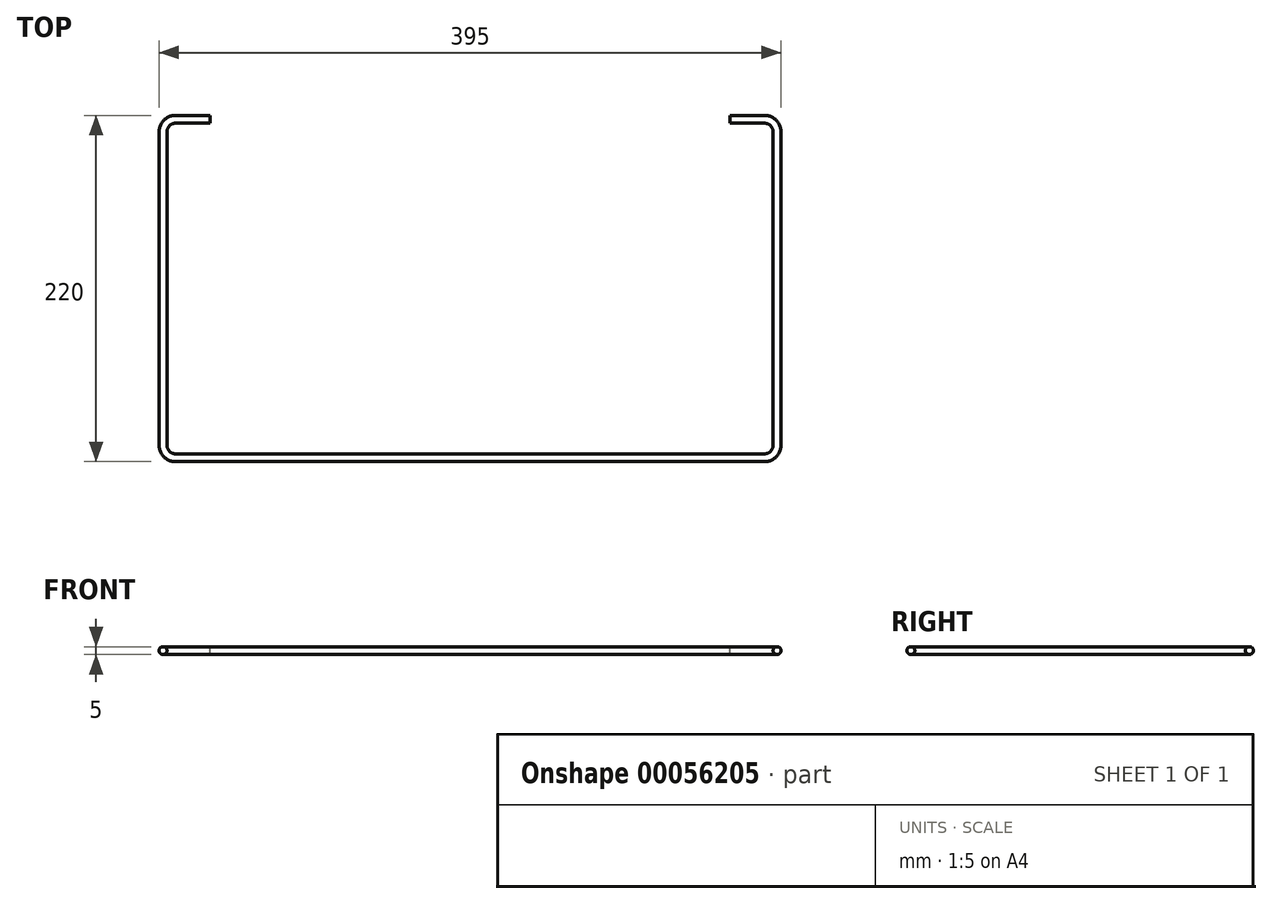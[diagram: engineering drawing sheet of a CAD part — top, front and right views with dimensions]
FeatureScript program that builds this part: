
annotation { "Feature Type Name" : "Feature", "Feature Type Description" : "" }
export const myFeature = defineFeature(function(context is Context, id is Id, definition is map)
    precondition{}
    {
        {
            var Q0;
            Q0=qCreatedBy(makeId("Top.planeOp"),FACE);
            var sketch = newSketch(context, id + "F0", { "sketchPlane" : qUnion([Q0])});
            skLineSegment(sketch, "E0.top", {"start": v(-22, -215) * mm, "end": v(352, -215) * mm});
            skLineSegment(sketch, "E0.left", {"start": v(-30, -8) * mm, "end": v(-30, -207) * mm});
            skLineSegment(sketch, "E0.right", {"start": v(360, -8) * mm, "end": v(360, -207) * mm});
            skPoint(sketch, "E1.visualSharp", {"position": v(-30, -215) * mm});
            skArc(sketch, "E1.filletArc", {"start": v(-30, -207) * mm, "mid": v(-27.66, -212.66) * mm, "end": v(-22, -215) * mm});
            skPoint(sketch, "E2.visualSharp", {"position": v(360, -215) * mm});
            skArc(sketch, "E2.filletArc", {"start": v(352, -215) * mm, "mid": v(357.66, -212.66) * mm, "end": v(360, -207) * mm});
            skLineSegment(sketch, "E3", {"start": v(-22, 0) * mm, "end": v(0, 0) * mm});
            skLineSegment(sketch, "E4", {"start": v(352, 0) * mm, "end": v(330, 0) * mm});
            skPoint(sketch, "E5.visualSharp", {"position": v(-30, 0) * mm});
            skArc(sketch, "E5.filletArc", {"start": v(-22, 0) * mm, "mid": v(-27.66, -2.34) * mm, "end": v(-30, -8) * mm});
            skPoint(sketch, "E6.visualSharp", {"position": v(360, 0) * mm});
            skArc(sketch, "E6.filletArc", {"start": v(360, -8) * mm, "mid": v(357.66, -2.34) * mm, "end": v(352, 0) * mm});
            skSolve(sketch);
        }
        {
            var Q0;
            Q0=qCreatedBy(makeId("Right.planeOp"),FACE);
            var sketch = newSketch(context, id + "F1", { "sketchPlane" : qUnion([Q0])});
            skCircle(sketch, "E7", {"center": v(0, 0) * mm, "radius": 2.5 * mm});
            skSolve(sketch);
        }
        {
            var Q0;
            Q0=makeQuery(id+"F1.imprint","IMPRINT",FACE,{"disambiguationData":[TD([[makeQuery(id+"F1.imprint","IMPRINT",EDGE,{"derivedFrom":sQuery(id+"F1.wireOp",EDGE,"E7")}),1.0]])]});
            var Q1;
            Q1=sQuery(id+"F0.wireOp",EDGE,"E0.left");
            var Q2;
            Q2=sQuery(id+"F0.wireOp",EDGE,"E5.filletArc");
            var Q3;
            Q3=sQuery(id+"F0.wireOp",EDGE,"E3");
            var Q4;
            Q4=sQuery(id+"F0.wireOp",EDGE,"E1.filletArc");
            var Q5;
            Q5=sQuery(id+"F0.wireOp",EDGE,"E0.top");
            var Q6;
            Q6=sQuery(id+"F0.wireOp",EDGE,"E2.filletArc");
            var Q7;
            Q7=sQuery(id+"F0.wireOp",EDGE,"E0.right");
            var Q8;
            Q8=sQuery(id+"F0.wireOp",EDGE,"E6.filletArc");
            var Q9;
            Q9=sQuery(id+"F0.wireOp",EDGE,"E4");
            sweep(context, id + "F2", {"profiles" : qUnion([Q0]), "path" : qUnion([Q1, Q2, Q3, Q4, Q5, Q6, Q7, Q8, Q9])});
        }
    });
